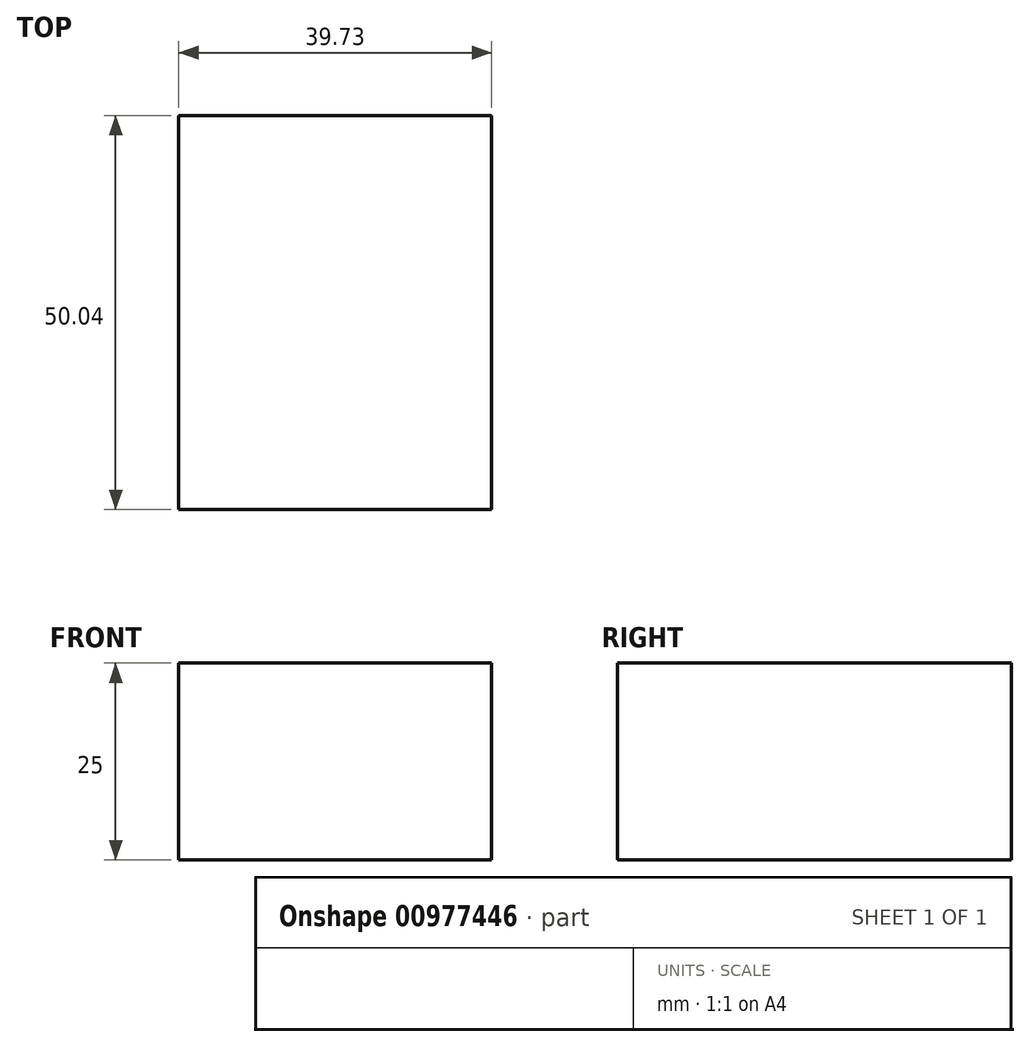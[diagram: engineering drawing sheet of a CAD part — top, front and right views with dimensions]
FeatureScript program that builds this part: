
annotation { "Feature Type Name" : "Feature", "Feature Type Description" : "" }
export const myFeature = defineFeature(function(context is Context, id is Id, definition is map)
    precondition{}
    {
        {
            var Q0;
            Q0=qCreatedBy(makeId("Top.planeOp"),FACE);
            var sketch = newSketch(context, id + "F0", { "sketchPlane" : qUnion([Q0])});
            skLineSegment(sketch, "E0.bottom", {"start": v(0, 0) * mm, "end": v(39.73, 0) * mm});
            skLineSegment(sketch, "E0.top", {"start": v(0, -50.04) * mm, "end": v(39.73, -50.04) * mm});
            skLineSegment(sketch, "E0.left", {"start": v(0, 0) * mm, "end": v(0, -50.04) * mm});
            skLineSegment(sketch, "E0.right", {"start": v(39.73, 0) * mm, "end": v(39.73, -50.04) * mm});
            skSolve(sketch);
        }
        {
            var Q0;
            Q0=makeQuery(id+"F0.imprint","IMPRINT",FACE,{"disambiguationData":[TD([[makeQuery(id+"F0.imprint","IMPRINT",EDGE,{"derivedFrom":sQuery(id+"F0.wireOp",EDGE,"E0.bottom")}),-1.0]])]});
            extrude(context, id + "F1", {"entities" : qUnion([Q0]), "depth" : 25 * mm, "offsetDistance" : 25 * mm});
        }
    });
